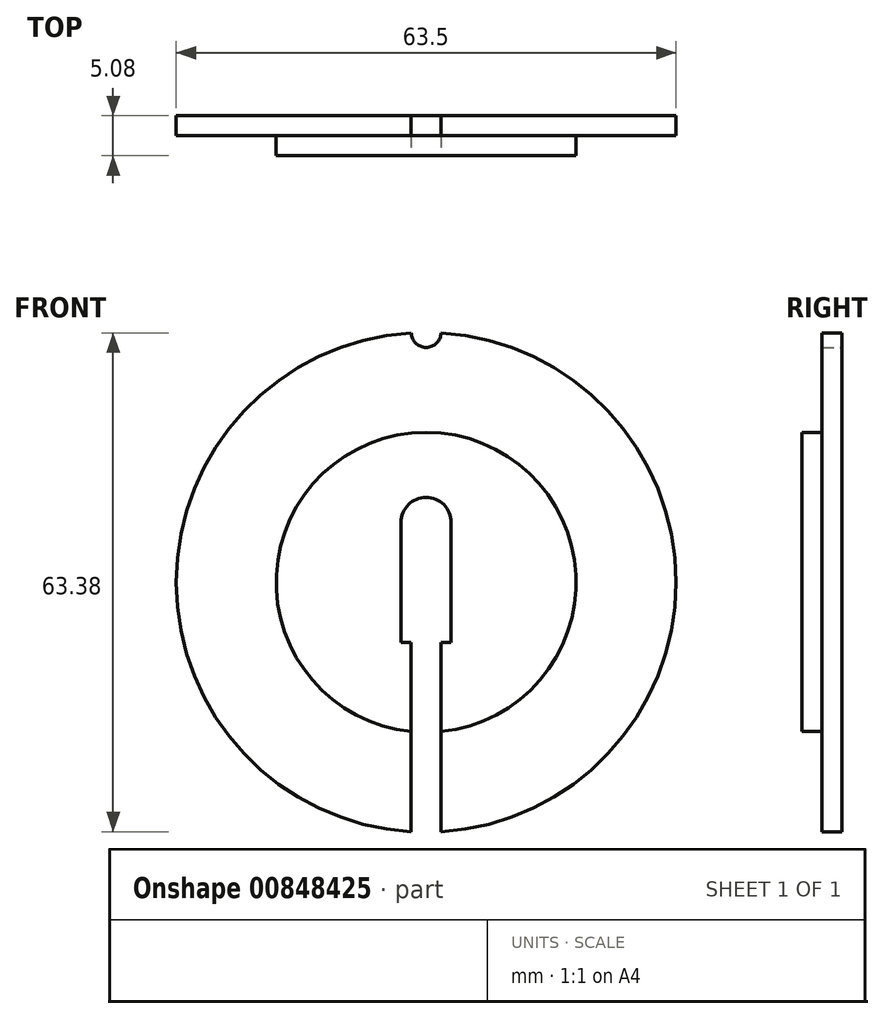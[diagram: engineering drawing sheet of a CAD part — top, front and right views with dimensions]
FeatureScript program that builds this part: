
annotation { "Feature Type Name" : "Feature", "Feature Type Description" : "" }
export const myFeature = defineFeature(function(context is Context, id is Id, definition is map)
    precondition{}
    {
        {
            var Q0;
            Q0=qCreatedBy(makeId("Front.planeOp"),FACE);
            var sketch = newSketch(context, id + "F0", { "sketchPlane" : qUnion([Q0])});
            skCircle(sketch, "E0", {"center": v(0, 0) * mm, "radius": 31.75 * mm});
            skCircle(sketch, "E1", {"center": v(0, 31.75) * mm, "radius": 1.9 * mm});
            skLineSegment(sketch, "E2", {"start": v(3.17, 7.62) * mm, "end": v(3.18, -7.62) * mm});
            skLineSegment(sketch, "E3", {"start": v(3.18, -7.62) * mm, "end": v(1.9, -7.62) * mm});
            skLineSegment(sketch, "E4", {"start": v(1.9, -7.62) * mm, "end": v(1.9, -36.61) * mm});
            skLineSegment(sketch, "E5", {"start": v(-3.18, 7.62) * mm, "end": v(-3.17, -7.62) * mm});
            skLineSegment(sketch, "E6", {"start": v(-3.17, -7.62) * mm, "end": v(-1.9, -7.62) * mm});
            skLineSegment(sketch, "E7", {"start": v(-1.9, -7.62) * mm, "end": v(-1.9, -36.61) * mm});
            skLineSegment(sketch, "E8", {"start": v(-33.76, 7.62) * mm, "end": v(34, 7.62) * mm, "construction": true});
            skArc(sketch, "E9", {"start": v(3.17, 7.62) * mm, "mid": v(0, 10.8) * mm, "end": v(-3.18, 7.62) * mm});
            skLineSegment(sketch, "E10", {"start": v(1.9, -36.61) * mm, "end": v(0, -36.61) * mm});
            skLineSegment(sketch, "E11", {"start": v(-1.9, -36.61) * mm, "end": v(0, -36.61) * mm});
            skSolve(sketch);
        }
        {
            var Q0;
            Q0=makeQuery(id+"F0.imprint","IMPRINT",FACE,{"disambiguationData":[TD([[makeQuery(id+"F0.imprint","IMPRINT",EDGE,{"derivedFrom":sQuery(id+"F0.wireOp",EDGE,"E2")}),1.0]])]});
            extrude(context, id + "F1", {"entities" : qUnion([Q0]), "depth" : 5.08 * mm, "offsetDistance" : 25.4 * mm});
        }
        {
            var Q0;
            Q0=makeQuery(id+"F1.opExtrude","CAP_FACE",FACE,{"disambiguationData":[OSD([sQuery(id+"F0.wireOp",EDGE,"E0"),sQuery(id+"F0.wireOp",EDGE,"E1"),sQuery(id+"F0.wireOp",EDGE,"E2"),sQuery(id+"F0.wireOp",EDGE,"E3"),sQuery(id+"F0.wireOp",EDGE,"E4"),sQuery(id+"F0.wireOp",EDGE,"E5"),sQuery(id+"F0.wireOp",EDGE,"E6"),sQuery(id+"F0.wireOp",EDGE,"E7"),sQuery(id+"F0.wireOp",EDGE,"E9")])],"isStart":false});
            var sketch = newSketch(context, id + "F2", { "sketchPlane" : qUnion([Q0])});
            skCircle(sketch, "E12", {"center": v(0, 0) * mm, "radius": 76.2 * mm});
            skCircle(sketch, "E13", {"center": v(0, 0) * mm, "radius": 19.05 * mm});
            skSolve(sketch);
        }
        {
            var Q0;
            Q0 = qSketchRegion(id + "F2", true);
            extrude(context, id + "F3", {"entities" : qUnion([Q0]), "operationType" : NewBodyOperationType.REMOVE, "oppositeDirection" : true, "depth" : 2.54 * mm, "offsetDistance" : 25.4 * mm});
        }
    });
